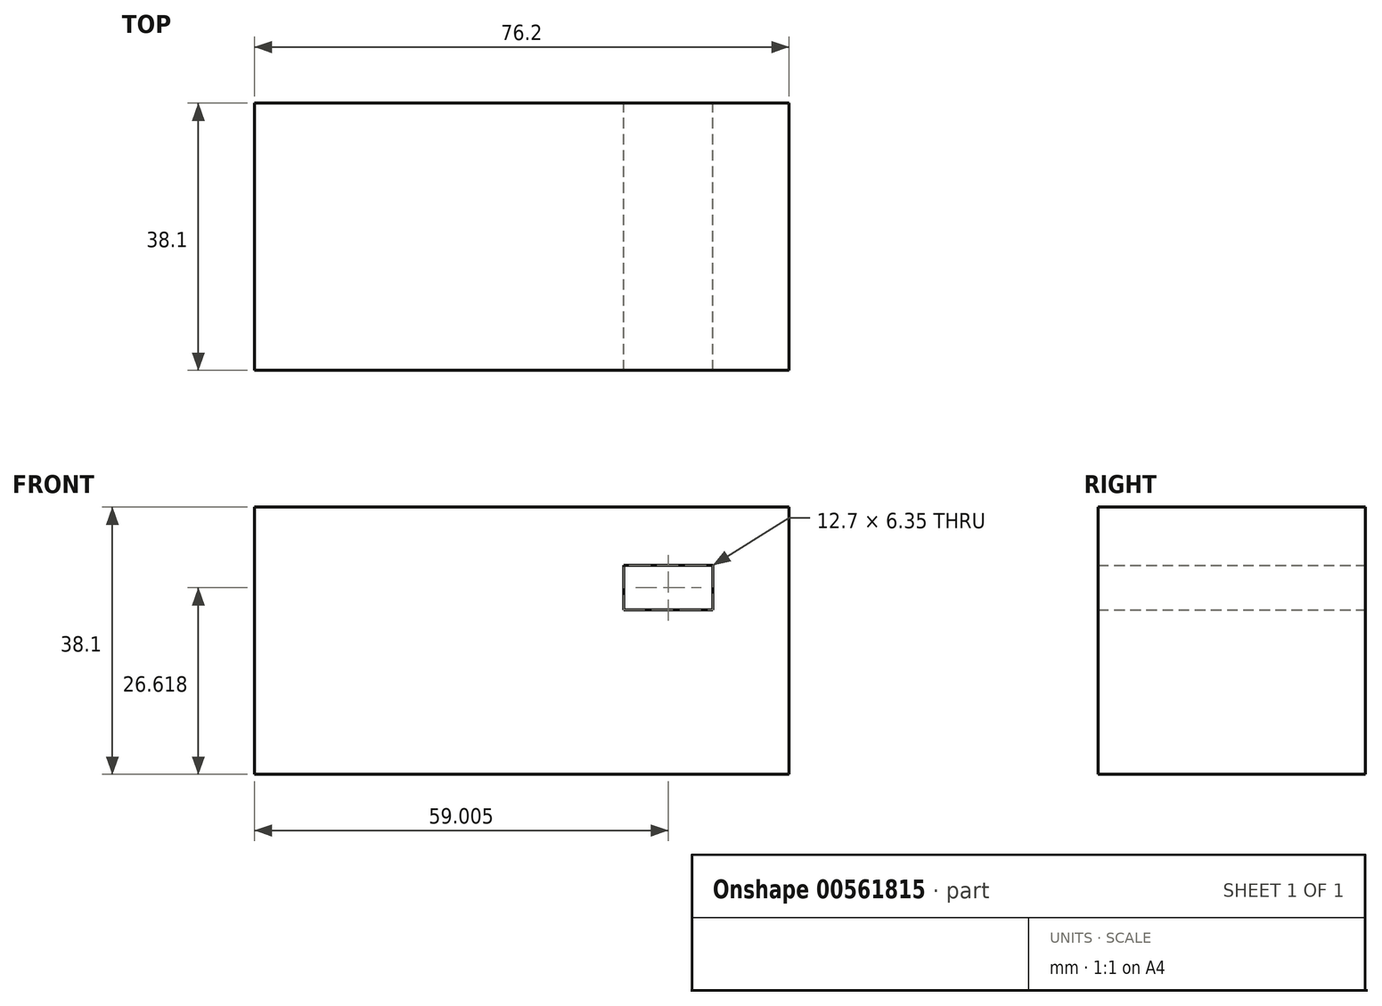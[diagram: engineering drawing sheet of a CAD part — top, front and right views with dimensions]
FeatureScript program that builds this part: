
annotation { "Feature Type Name" : "Feature", "Feature Type Description" : "" }
export const myFeature = defineFeature(function(context is Context, id is Id, definition is map)
    precondition{}
    {
        {
            var Q0;
            Q0=qCreatedBy(makeId("Front.planeOp"),FACE);
            var sketch = newSketch(context, id + "F0", { "sketchPlane" : qUnion([Q0])});
            skLineSegment(sketch, "E0.bottom", {"start": v(-45.3, 40.67) * mm, "end": v(30.9, 40.67) * mm});
            skLineSegment(sketch, "E0.top", {"start": v(-45.3, 2.57) * mm, "end": v(30.9, 2.57) * mm});
            skLineSegment(sketch, "E0.left", {"start": v(-45.3, 40.67) * mm, "end": v(-45.3, 2.57) * mm});
            skLineSegment(sketch, "E0.right", {"start": v(30.9, 40.67) * mm, "end": v(30.9, 2.57) * mm});
            skSolve(sketch);
        }
        {
            var Q0;
            Q0 = qSketchRegion(id + "F0", true);
            extrude(context, id + "F1", {"entities" : qUnion([Q0]), "depth" : 38.1 * mm, "offsetDistance" : 25.4 * mm});
        }
        {
            var Q0;
            Q0=qCreatedBy(makeId("Front.planeOp"),FACE);
            var sketch = newSketch(context, id + "F2", { "sketchPlane" : qUnion([Q0])});
            skLineSegment(sketch, "E1.bottom", {"start": v(7.35, 32.36) * mm, "end": v(20.05, 32.36) * mm});
            skLineSegment(sketch, "E1.top", {"start": v(7.35, 26.01) * mm, "end": v(20.05, 26.01) * mm});
            skLineSegment(sketch, "E1.left", {"start": v(7.35, 32.36) * mm, "end": v(7.35, 26.01) * mm});
            skLineSegment(sketch, "E1.right", {"start": v(20.05, 32.36) * mm, "end": v(20.05, 26.01) * mm});
            skSolve(sketch);
        }
        {
            var Q0;
            Q0 = qSketchRegion(id + "F2", true);
            extrude(context, id + "F3", {"entities" : qUnion([Q0]), "operationType" : NewBodyOperationType.REMOVE, "depth" : 44.2 * mm, "offsetDistance" : 25.4 * mm});
        }
    });
